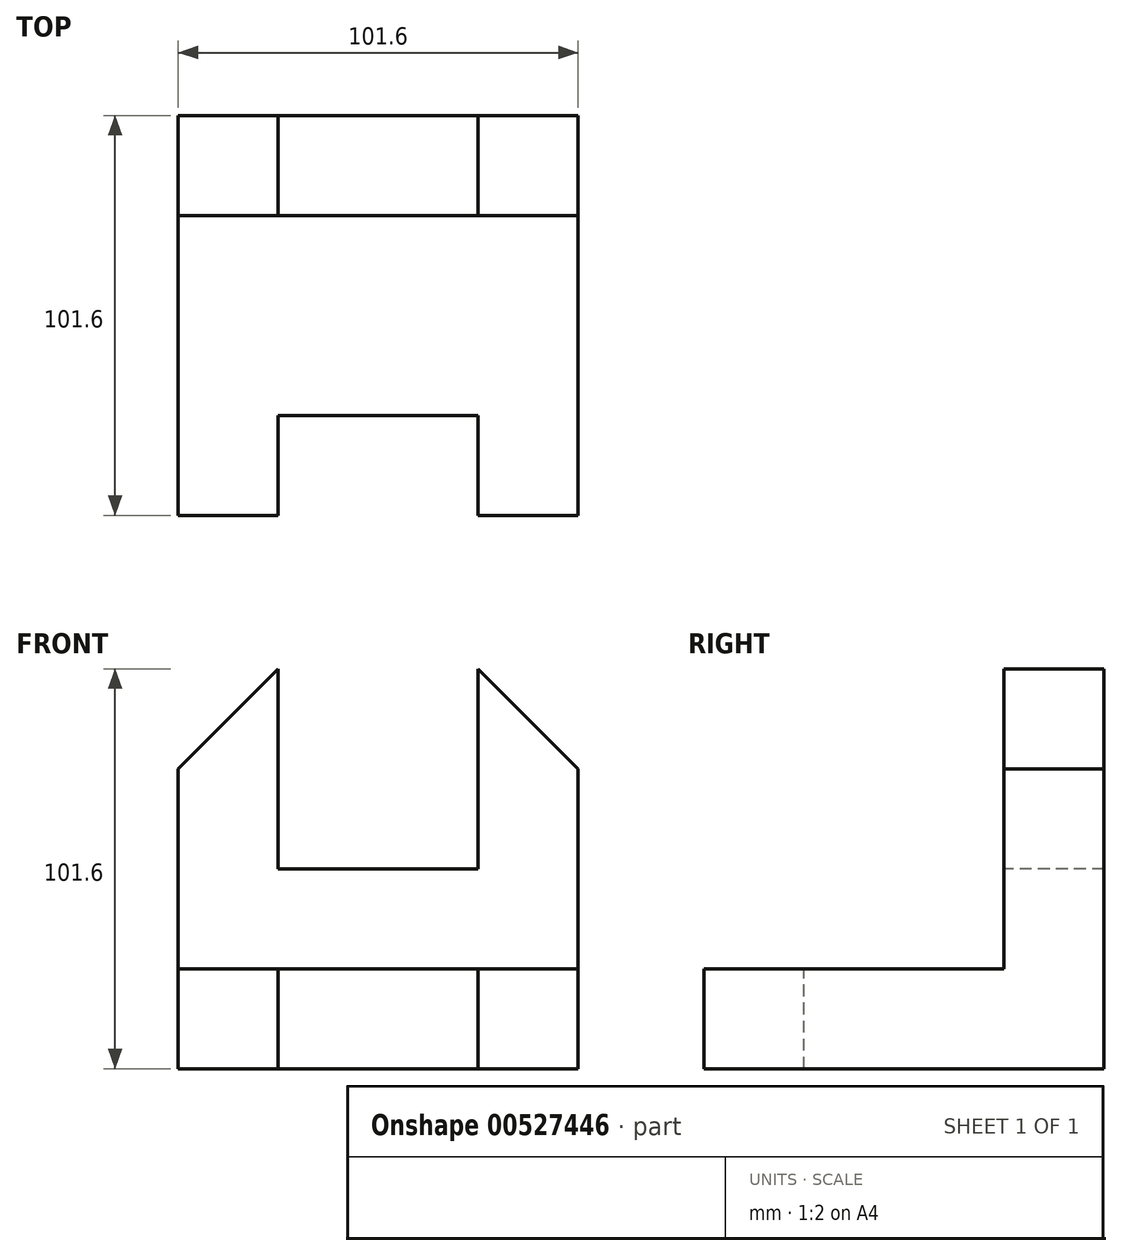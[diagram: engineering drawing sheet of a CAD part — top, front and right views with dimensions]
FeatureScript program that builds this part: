
annotation { "Feature Type Name" : "Feature", "Feature Type Description" : "" }
export const myFeature = defineFeature(function(context is Context, id is Id, definition is map)
    precondition{}
    {
        {
            var Q0;
            Q0=qCreatedBy(makeId("Right.planeOp"),FACE);
            var sketch = newSketch(context, id + "F0", { "sketchPlane" : qUnion([Q0])});
            skLineSegment(sketch, "E0", {"start": v(0, 0) * mm, "end": v(-76.2, 0) * mm});
            skLineSegment(sketch, "E1", {"start": v(-76.2, 0) * mm, "end": v(-76.2, -25.4) * mm});
            skLineSegment(sketch, "E2", {"start": v(-76.2, -25.4) * mm, "end": v(25.4, -25.4) * mm});
            skLineSegment(sketch, "E3", {"start": v(25.4, -25.4) * mm, "end": v(25.4, 76.2) * mm});
            skLineSegment(sketch, "E4", {"start": v(25.4, 76.2) * mm, "end": v(0, 76.2) * mm});
            skLineSegment(sketch, "E5", {"start": v(0, 76.2) * mm, "end": v(0, 0) * mm});
            skSolve(sketch);
        }
        {
            var Q0;
            Q0=makeQuery(id+"F0.imprint","IMPRINT",FACE,{"disambiguationData":[TD([[makeQuery(id+"F0.imprint","IMPRINT",EDGE,{"derivedFrom":sQuery(id+"F0.wireOp",EDGE,"E0")}),1.0]])]});
            extrude(context, id + "F1", {"entities" : qUnion([Q0]), "depth" : 101.6 * mm, "offsetDistance" : 25.4 * mm});
        }
        {
            var Q0;
            Q0=makeQuery(id+"F1.opExtrude","SWEPT_FACE",FACE,{"disambiguationData":[OSD([sQuery(id+"F0.wireOp",EDGE,"E0")])]});
            var sketch = newSketch(context, id + "F2", { "sketchPlane" : qUnion([Q0])});
            skLineSegment(sketch, "E6", {"start": v(0, -76.2) * mm, "end": v(25.4, -76.2) * mm});
            skLineSegment(sketch, "E7", {"start": v(25.4, -76.2) * mm, "end": v(25.4, -50.8) * mm});
            skLineSegment(sketch, "E8", {"start": v(25.4, -50.8) * mm, "end": v(76.2, -50.8) * mm});
            skLineSegment(sketch, "E9", {"start": v(76.2, -50.8) * mm, "end": v(76.2, -76.2) * mm});
            skSolve(sketch);
        }
        {
            var Q0;
            {var subQ0=sQuery(id+"F2.wireOp",EDGE,"E7");Q0=makeQuery(id+"F2.imprint","IMPRINT",FACE,{"disambiguationData":[TD([[makeQuery(id+"F2.imprint","IMPRINT",EDGE,{"derivedFrom":subQ0}),-1.0]])]});}
            extrude(context, id + "F3", {"entities" : qUnion([Q0]), "operationType" : NewBodyOperationType.REMOVE, "oppositeDirection" : true, "depth" : 25.4 * mm, "offsetDistance" : 25.4 * mm});
        }
        {
            var Q0;
            Q0=makeQuery(id+"F1.opExtrude","SWEPT_FACE",FACE,{"disambiguationData":[OSD([sQuery(id+"F0.wireOp",EDGE,"E5")])]});
            var sketch = newSketch(context, id + "F4", { "sketchPlane" : qUnion([Q0])});
            skLineSegment(sketch, "E10", {"start": v(0, 0) * mm, "end": v(0, 25.4) * mm});
            skLineSegment(sketch, "E11", {"start": v(0, 25.4) * mm, "end": v(25.4, 25.4) * mm});
            skLineSegment(sketch, "E12", {"start": v(25.4, 25.4) * mm, "end": v(25.4, 76.2) * mm});
            skLineSegment(sketch, "E13", {"start": v(25.4, 76.2) * mm, "end": v(76.2, 76.2) * mm});
            skLineSegment(sketch, "E14", {"start": v(76.2, 76.2) * mm, "end": v(76.2, 25.4) * mm});
            skLineSegment(sketch, "E15", {"start": v(76.2, 25.4) * mm, "end": v(101.6, 25.4) * mm});
            skLineSegment(sketch, "E16", {"start": v(25.4, 25.4) * mm, "end": v(76.2, 25.4) * mm});
            skSolve(sketch);
        }
        {
            var Q0;
            Q0=makeQuery(id+"F4.imprint","IMPRINT",FACE,{"disambiguationData":[TD([[makeQuery(id+"F4.imprint","IMPRINT",EDGE,{"derivedFrom":sQuery(id+"F4.wireOp",EDGE,"E12")}),-1.0]])]});
            extrude(context, id + "F5", {"entities" : qUnion([Q0]), "operationType" : NewBodyOperationType.REMOVE, "oppositeDirection" : true, "depth" : 25.4 * mm, "offsetDistance" : 25.4 * mm});
        }
        {
            var Q0;
            Q0=makeQuery(id+"F1.opExtrude","SWEPT_FACE",FACE,{"disambiguationData":[OSD([sQuery(id+"F0.wireOp",EDGE,"E5")])]});
            var sketch = newSketch(context, id + "F6", { "sketchPlane" : qUnion([Q0])});
            skLineSegment(sketch, "E17", {"start": v(76.2, 76.2) * mm, "end": v(76.2, 25.4) * mm});
            skLineSegment(sketch, "E18", {"start": v(101.6, 25.4) * mm, "end": v(101.6, 50.8) * mm});
            skLineSegment(sketch, "E19", {"start": v(25.4, 25.4) * mm, "end": v(25.4, 50.8) * mm});
            skLineSegment(sketch, "E20", {"start": v(101.6, 50.8) * mm, "end": v(76.2, 76.2) * mm});
            skLineSegment(sketch, "E21", {"start": v(25.4, 50.8) * mm, "end": v(0, 50.8) * mm});
            skLineSegment(sketch, "E22", {"start": v(25.4, 76.2) * mm, "end": v(0, 50.8) * mm});
            skSolve(sketch);
        }
        {
            var Q0;
            {var subQ0=sQuery(id+"F6.wireOp",EDGE,"E22");Q0=makeQuery(id+"F6.imprint","IMPRINT",FACE,{"disambiguationData":[TD([[makeQuery(id+"F6.imprint","IMPRINT",EDGE,{"derivedFrom":subQ0}),-1.0]])]});}
            var Q1;
            {var subQ0=sQuery(id+"F6.wireOp",EDGE,"E20");Q1=makeQuery(id+"F6.imprint","IMPRINT",FACE,{"disambiguationData":[TD([[makeQuery(id+"F6.imprint","IMPRINT",EDGE,{"derivedFrom":subQ0}),-1.0]])]});}
            extrude(context, id + "F7", {"entities" : qUnion([Q0, Q1]), "operationType" : NewBodyOperationType.REMOVE, "oppositeDirection" : true, "depth" : 25.4 * mm, "offsetDistance" : 25.4 * mm});
        }
    });
